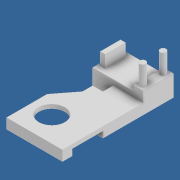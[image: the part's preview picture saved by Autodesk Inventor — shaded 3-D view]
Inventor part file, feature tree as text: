
AUTODESK INVENTOR PART (.ipt)
format: ipt  version: 2020 (Build 240168000, 168)  size: 225,792 bytes
history: native  units: mm
features: extrude x13, sketch x13, other x2, chamfer x1, loft x1, projected_geometry x1
ambient origin geometry x8: Origin, YZ Plane, XZ Plane, XY Plane, X Axis, Y Axis, Z Axis, Center Point
bodies: Solid1 (feature_tree)
feature tree (31):
  extrude  "Extrusion1"  Depth=23.8mm
  extrude  "Extrusion2"  Depth=16.0mm
  extrude  "Extrusion3"  Depth=8.0mm TaperAngle=0.0deg
  chamfer  "Chamfer1"  Distance=5.0mm
  extrude  "Extrusion4"  Depth=16.0mm
  extrude  "Extrusion5"  Depth=32.0mm TaperAngle=0.0deg
  extrude  "Extrusion6"  Depth=7.6mm
  sketch  "Sketch9"  dims[d13=8.0mm d14=2.0mm d15=45.0deg d18=16.0mm]
  extrude  "Extrusion7"  Depth=31.8mm TaperAngle=0.0deg
  extrude  "Extrusion8"  Depth=4.7mm
  extrude  "Extrusion9"  Depth=19.8mm
  extrude  "Extrusion10"  Depth=23.8mm
  extrude  "Extrusion11"  Depth=8.0mm
  extrude  "Extrusion12"  Depth=16.0mm TaperAngle=0.0deg
  loft  "Loft1"
  extrude  "Extrusion13"  Depth=24.0mm TaperAngle=0.0deg
  sketch  "Sketch1"  dims[d0=24.0mm d1=23.8mm]
  sketch  "Sketch3"  dims[d2=8.0mm d3=0.0mm d4=16.0mm]
  sketch  "Sketch4"  dims[d5=3.0mm d6=8.0mm d7=0.0mm]
  sketch  "Sketch6"  dims[d8=4.7mm]
  sketch  "Sketch7"  dims[d9=4.3mm]
  sketch  "Sketch8"  dims[d10=4.0mm d11=5.0mm d12=0.0mm]
  sketch  "Sketch10"  dims[d19=3.0mm d20=32.0mm d21=0.0mm]
  sketch  "Sketch11"  dims[d22=16.0mm d23=7.6mm]
  sketch  "Sketch12"  dims[d24=5.0mm d25=0.0mm d26=31.8mm d27=0.0mm]
  sketch  "Sketch13"  dims[d28=4.7mm d29=4.7mm]
  projected_geometry  "Projected Loop1"
  sketch  "Sketch14"  dims[d30=16.0mm d32=19.8mm]
  other  "Edges1"
  other  "Edges2"
  sketch  "Sketch15"  dims[d33=11.8mm d34=23.8mm d35=8.0mm d36=16.0mm d37=0.0mm d38=4.4mm d39=0.0mm d40=24.0mm d41=0.0mm d42=8.0mm d43=23.8mm d44=4.0mm d45=0.0mm d46=28.2mm d47=0.0mm d48=20.5mm d49=16.0mm d51=19.8mm d52=3.0mm d53=0.0mm d54=0.0mm d55=90.0deg d56=0.0mm d57=90.0deg d58=4.0mm d59=16.0mm d60=4.0mm d61=2.0mm d62=10.0mm d63=0.0mm]
